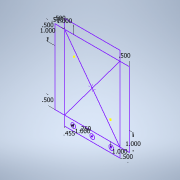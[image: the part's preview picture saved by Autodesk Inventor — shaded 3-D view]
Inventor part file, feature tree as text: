
AUTODESK INVENTOR PART (.ipt)
format: ipt  version: 2020 (Build 240168000, 168)  size: 232,960 bytes
history: native  units: in
note: dims shown in document units (in); Inventor stores cm internally (conversion verified against a paired STEP export)
features: other x6, reference x5, extrude x1, sketch x1
ambient origin geometry x8: Origin, YZ Plane, XZ Plane, XY Plane, X Axis, Y Axis, Z Axis, Center Point
bodies: Solid1 (feature_tree)
feature tree (13):
  extrude  "Extrusion1"  Depth=0.1in
  sketch  "Sketch1"  dims[d0=1.0in d1=1.0in d2=1.0in d3=1.0in d4=0.5in d5=0.5in d6=0.5in d7=0.5in d8=0.5in d9=0.5in d10=0.25in d11=0.4545in d12=1.1811in d14=1.0in d15=0.3937in d17=1.0in d21=0.25in d22=1.1811in d24=1.0in d25=0.3937in d27=1.0in d29=0.25in d30=1.5748in d32=1.0in d33=0.3937in d35=1.0in d37=0.25in d38=1.5748in d40=1.0in d41=0.3937in d43=1.0in d45=0.1in d46=0.0in]
  reference  "Reference1"
  reference  "Reference2"
  reference  "Reference3"
  reference  "Reference4"
  reference  "Reference5"
  other  "<userpath>\Documents\Inventor\Drone\Assembly.iam"
  other  "Assembly.iam"
  other  "standoff:4"
  other  "standoff:2"
  other  "standoff:3"
  other  "standoff:1"
